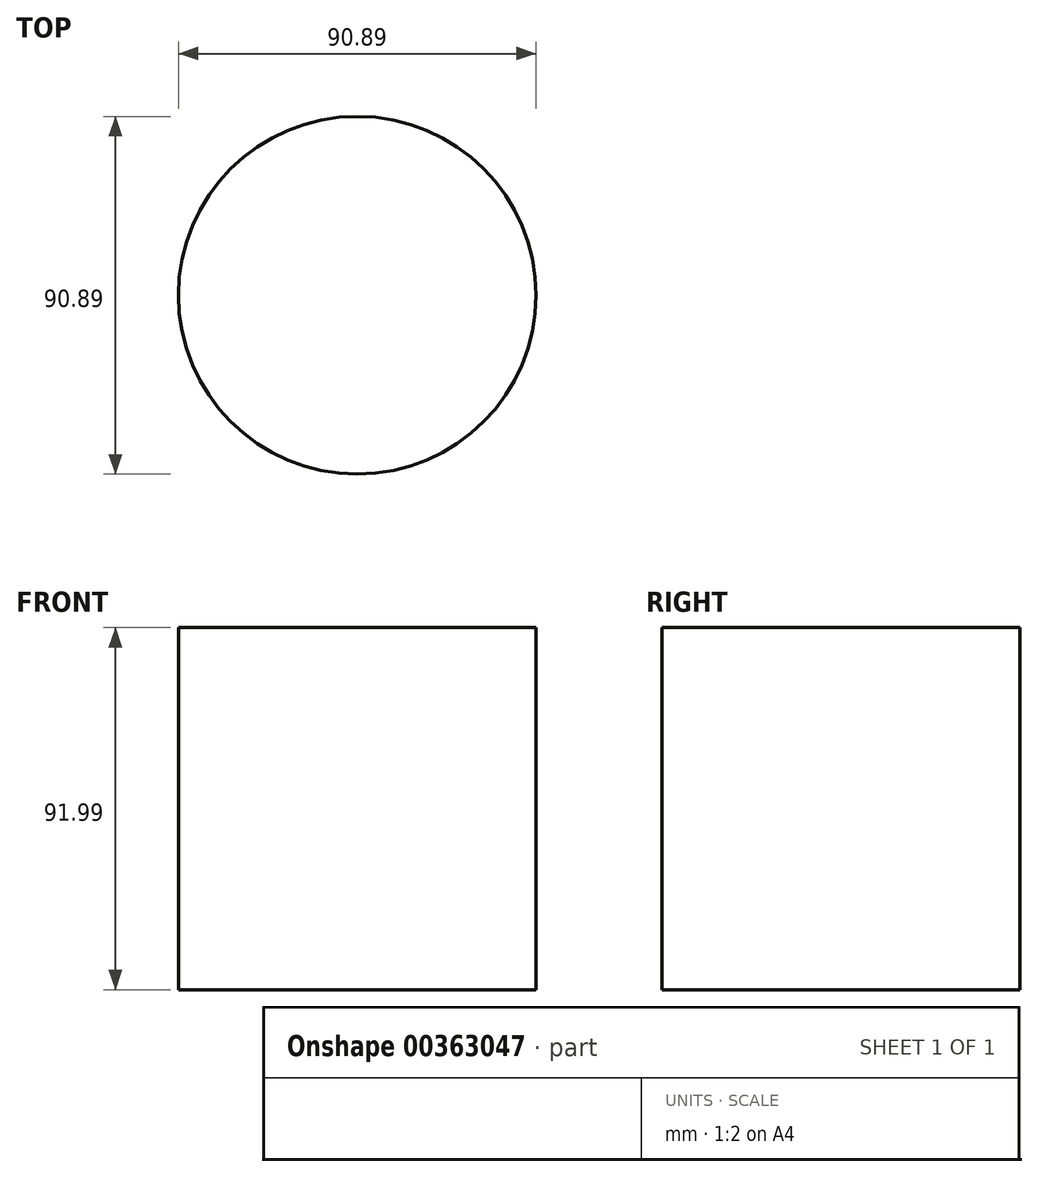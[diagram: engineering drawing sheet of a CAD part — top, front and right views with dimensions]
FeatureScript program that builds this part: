
annotation { "Feature Type Name" : "Feature", "Feature Type Description" : "" }
export const myFeature = defineFeature(function(context is Context, id is Id, definition is map)
    precondition{}
    {
        {
            var Q0;
            Q0=qCreatedBy(makeId("Top.planeOp"),FACE);
            var sketch = newSketch(context, id + "F0", { "sketchPlane" : qUnion([Q0])});
            skCircle(sketch, "E0", {"center": v(16.48, -57.01) * mm, "radius": 45.44 * mm});
            skPoint(sketch, "E0.first.point", {"position": v(6.88, -12.6) * mm});
            skPoint(sketch, "E0.second.point", {"position": v(58.56, -39.87) * mm});
            skPoint(sketch, "E0.third.point", {"position": v(0, -99.36) * mm});
            skSolve(sketch);
        }
        {
            var Q0;
            Q0=makeQuery(id+"F0.imprint","IMPRINT",FACE,{"disambiguationData":[TD([[makeQuery(id+"F0.imprint","IMPRINT",EDGE,{"derivedFrom":sQuery(id+"F0.wireOp",EDGE,"E0")}),1.0]])]});
            var sketch = newSketch(context, id + "F1", { "sketchPlane" : qUnion([Q0])});
            skSolve(sketch);
        }
        {
            var Q0;
            Q0=makeQuery(id+"F1.imprint","IMPRINT",FACE,{"disambiguationData":[TD([[makeQuery(id+"F1.imprint","IMPRINT",EDGE,{"derivedFrom":makeQuery(id+"F0.imprint","IMPRINT",EDGE,{"derivedFrom":sQuery(id+"F0.wireOp",EDGE,"E0")})}),1.0]])]});
            extrude(context, id + "F2", {"entities" : qUnion([Q0]), "depth" : 92 * mm});
        }
    });
